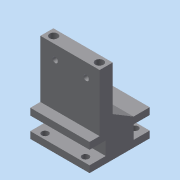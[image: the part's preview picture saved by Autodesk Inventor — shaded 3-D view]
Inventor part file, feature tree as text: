
AUTODESK INVENTOR PART (.ipt)
format: ipt  version: 2015 (Build 190159000, 159)  size: 189,952 bytes
history: native  units: mm
features: sketch x10, extrude x7, hole x3, projected_geometry x2, plane x1, chamfer x1
ambient origin geometry x8: Origin, YZ Plane, XZ Plane, XY Plane, X Axis, Y Axis, Z Axis, Center Point
bodies: Solid1 (feature_tree)
feature tree (24):
  extrude  "Extrusion1"  Depth=6.0mm
  hole  "Hole1"  [1 undecoded]
  hole  "Hole2"  [1 undecoded]
  extrude  "Extrusion2"  Depth=10.0mm
  extrude  "Extrusion3"  Depth=10.0mm
  plane  "Work Plane2"
  extrude  "Extrusion4"  Depth=7.5mm
  hole  "Hole3"  [1 undecoded]
  extrude  "Extrusion5"  Depth=10.0mm
  chamfer  "Chamfer1"  Distance=12.0mm
  extrude  "Extrusion6"  Depth=12.0mm
  extrude  "Extrusion7"  Depth=10.0mm TaperAngle=0.0deg
  sketch  "Sketch1"  dims[d0=6.0mm d1=6.0mm]
  sketch  "Sketch2"  dims[d2=34.0mm d3=44.0mm]
  sketch  "Sketch3"  dims[d4=5.0mm d5=42.5mm d6=0.0mm]
  sketch  "Sketch4"  dims[d10=4.0mm d11=6.0mm d12=4.0mm d13=2.0mm d14=90.0deg d15=10.0mm d16=20.594885mm d17=10.0mm]
  projected_geometry  "Projected Loop1"
  sketch  "Sketch5"  dims[d18=11.0mm d19=10.0mm]
  sketch  "Sketch6"  dims[d20=10.0mm]
  sketch  "Sketch7"  dims[d21=4.0mm d22=6.0mm d23=4.0mm d24=2.0mm d25=90.0deg d26=10.0mm d27=20.594885mm d28=7.5mm]
  sketch  "Sketch8"  dims[d29=27.5mm d30=20.0mm d31=0.0mm]
  sketch  "Sketch9"  dims[d32=20.0mm d33=0.0mm d34=10.0mm]
  projected_geometry  "Projected Loop2"
  sketch  "Sketch11"  dims[d35=5.0mm d36=12.0mm d37=12.0mm d38=10.0mm d39=0.0mm d40=4.0mm d41=4.0mm d42=4.0mm d43=4.0mm d44=7.0mm d45=7.0mm d46=7.0mm d47=7.0mm d48=4.0mm d49=6.0mm d50=5.0mm d51=6.0mm d52=90.0deg d53=16.0mm d54=20.594885mm d55=0.0mm d56=5.0mm d57=15.5mm d58=0.0mm d59=15.5mm d60=2.0mm d61=45.0deg d62=15.5mm d63=0.0mm d64=2.0mm d65=0.0mm]
note: 3 required parameter values undecoded (feature->parameter linkage not recoverable at this tier; creation-order binding heuristic only, values carry confidence <= 0.55)
